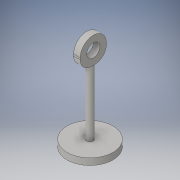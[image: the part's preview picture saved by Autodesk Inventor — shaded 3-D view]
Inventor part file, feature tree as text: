
AUTODESK INVENTOR PART (.ipt)
format: ipt  version: 2016 (Build 200138000, 138)  size: 142,848 bytes
history: native  units: mm
features: sketch x5, extrude x4, fillet x4
ambient origin geometry x8: Origin, YZ Plane, XZ Plane, XY Plane, X Axis, Y Axis, Z Axis, Center Point
bodies: Volumenkörper1 (feature_tree)
feature tree (13):
  extrude  "Extrusion1"  Depth=1.0mm TaperAngle=0.0deg
  extrude  "Extrusion2"  Depth=14.0mm TaperAngle=0.0deg
  extrude  "Extrusion4"  Depth=4.0mm
  extrude  "Extrusion5"  Depth=4.0mm TaperAngle=0.0deg
  sketch  "Skizze10"  dims[d47=2.0mm d48=2.0mm d49=1.75mm d50=1.75mm]
  fillet  "Rundung9"  Radius=2.0mm
  fillet  "Rundung10"  Radius=2.0mm
  fillet  "Rundung11"  Radius=2.0mm
  fillet  "Rundung12"  Radius=1.0mm
  sketch  "Skizze1"  dims[d0=7.0mm d1=1.0mm d2=0.0mm]
  sketch  "Skizze2"  dims[d3=1.0mm d4=14.0mm d5=0.0mm]
  sketch  "Skizze4"  dims[d25=1.0mm d26=4.0mm]
  sketch  "Skizze6"  dims[d27=2.0mm d28=4.0mm d29=0.0mm d31=2.0mm d32=2.0mm d33=2.0mm d34=1.0mm d35=0.0mm]
